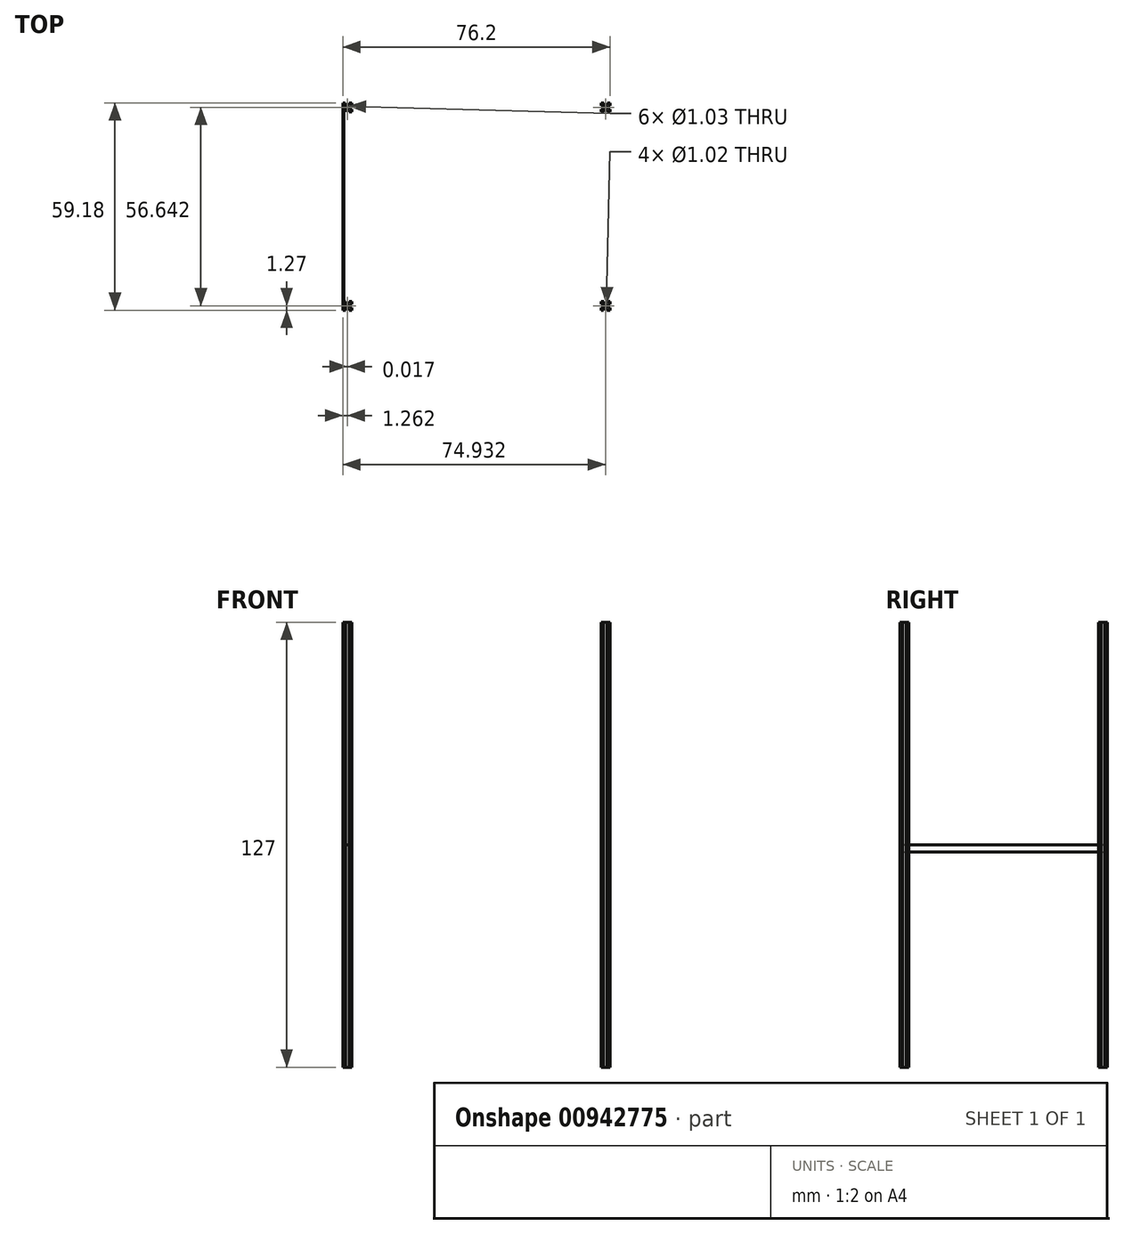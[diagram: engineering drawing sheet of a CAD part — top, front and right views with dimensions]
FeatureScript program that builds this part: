
annotation { "Feature Type Name" : "Feature", "Feature Type Description" : "" }
export const myFeature = defineFeature(function(context is Context, id is Id, definition is map)
    precondition{}
    {
        {
            var Q0;
            Q0=qCreatedBy(makeId("Top.planeOp"),FACE);
            var sketch = newSketch(context, id + "F0", { "sketchPlane" : qUnion([Q0])});
            skLineSegment(sketch, "E0.bottom", {"start": v(0, 0) * mm, "end": v(76.2, 0) * mm});
            skLineSegment(sketch, "E0.top", {"start": v(0, 59.18) * mm, "end": v(76.2, 59.18) * mm});
            skLineSegment(sketch, "E0.left", {"start": v(0, 0) * mm, "end": v(0, 59.18) * mm});
            skLineSegment(sketch, "E0.right", {"start": v(76.2, 0) * mm, "end": v(76.2, 59.18) * mm});
            skLineSegment(sketch, "E1.bottom", {"start": v(0, 59.18) * mm, "end": v(2.54, 59.18) * mm});
            skLineSegment(sketch, "E1.top", {"start": v(0, 56.64) * mm, "end": v(2.54, 56.64) * mm});
            skLineSegment(sketch, "E1.left", {"start": v(0, 59.18) * mm, "end": v(0, 56.64) * mm});
            skLineSegment(sketch, "E1.right", {"start": v(2.54, 59.18) * mm, "end": v(2.54, 56.64) * mm});
            skLineSegment(sketch, "E2.bottom", {"start": v(76.2, 59.18) * mm, "end": v(73.66, 59.18) * mm});
            skLineSegment(sketch, "E2.top", {"start": v(76.2, 56.64) * mm, "end": v(73.66, 56.64) * mm});
            skLineSegment(sketch, "E2.left", {"start": v(76.2, 59.18) * mm, "end": v(76.2, 56.64) * mm});
            skLineSegment(sketch, "E2.right", {"start": v(73.66, 59.18) * mm, "end": v(73.66, 56.64) * mm});
            skLineSegment(sketch, "E3.bottom", {"start": v(0, 0) * mm, "end": v(2.54, 0) * mm});
            skLineSegment(sketch, "E3.top", {"start": v(0, 2.54) * mm, "end": v(2.54, 2.54) * mm});
            skLineSegment(sketch, "E3.left", {"start": v(0, 0) * mm, "end": v(0, 2.54) * mm});
            skLineSegment(sketch, "E3.right", {"start": v(2.54, 0) * mm, "end": v(2.54, 2.54) * mm});
            skLineSegment(sketch, "E4.bottom", {"start": v(76.2, 0) * mm, "end": v(73.66, 0) * mm});
            skLineSegment(sketch, "E4.top", {"start": v(76.2, 2.54) * mm, "end": v(73.66, 2.54) * mm});
            skLineSegment(sketch, "E4.left", {"start": v(76.2, 0) * mm, "end": v(76.2, 2.54) * mm});
            skLineSegment(sketch, "E4.right", {"start": v(73.66, 0) * mm, "end": v(73.66, 2.54) * mm});
            skLineSegment(sketch, "E5", {"start": v(0, 57.91) * mm, "end": v(1.26, 57.91) * mm});
            skCircle(sketch, "E6", {"center": v(1.26, 57.91) * mm, "radius": 0.52 * mm});
            skLineSegment(sketch, "E7.bottom", {"start": v(0.74, 59.18) * mm, "end": v(1.79, 59.18) * mm});
            skLineSegment(sketch, "E7.top", {"start": v(0.74, 58.68) * mm, "end": v(1.79, 58.68) * mm});
            skLineSegment(sketch, "E7.left", {"start": v(0.74, 59.18) * mm, "end": v(0.74, 58.68) * mm});
            skLineSegment(sketch, "E7.right", {"start": v(1.79, 59.18) * mm, "end": v(1.79, 58.68) * mm});
            skLineSegment(sketch, "E8.bottom", {"start": v(2.54, 58.42) * mm, "end": v(2.04, 58.42) * mm});
            skLineSegment(sketch, "E8.top", {"start": v(2.54, 57.37) * mm, "end": v(2.04, 57.37) * mm});
            skLineSegment(sketch, "E8.left", {"start": v(2.54, 58.42) * mm, "end": v(2.54, 57.37) * mm});
            skLineSegment(sketch, "E8.right", {"start": v(2.04, 58.42) * mm, "end": v(2.04, 57.37) * mm});
            skLineSegment(sketch, "E9.bottom", {"start": v(0.74, 56.64) * mm, "end": v(1.79, 56.64) * mm});
            skLineSegment(sketch, "E9.top", {"start": v(0.74, 57.14) * mm, "end": v(1.79, 57.14) * mm});
            skLineSegment(sketch, "E9.left", {"start": v(0.74, 56.64) * mm, "end": v(0.74, 57.14) * mm});
            skLineSegment(sketch, "E9.right", {"start": v(1.79, 56.64) * mm, "end": v(1.79, 57.14) * mm});
            skLineSegment(sketch, "E10.bottom", {"start": v(0, 57.37) * mm, "end": v(0.5, 57.37) * mm});
            skLineSegment(sketch, "E10.top", {"start": v(0, 58.4) * mm, "end": v(0.5, 58.4) * mm});
            skLineSegment(sketch, "E10.left", {"start": v(0, 57.37) * mm, "end": v(0, 58.4) * mm});
            skLineSegment(sketch, "E10.right", {"start": v(0.5, 57.37) * mm, "end": v(0.5, 58.4) * mm});
            skLineSegment(sketch, "E11", {"start": v(73.66, 57.91) * mm, "end": v(74.93, 57.91) * mm});
            skCircle(sketch, "E12", {"center": v(74.93, 57.91) * mm, "radius": 0.5 * mm});
            skLineSegment(sketch, "E13.bottom", {"start": v(76.2, 58.39) * mm, "end": v(75.7, 58.39) * mm});
            skLineSegment(sketch, "E13.top", {"start": v(76.2, 57.38) * mm, "end": v(75.7, 57.38) * mm});
            skLineSegment(sketch, "E13.left", {"start": v(76.2, 58.39) * mm, "end": v(76.2, 57.38) * mm});
            skLineSegment(sketch, "E13.right", {"start": v(75.7, 58.39) * mm, "end": v(75.7, 57.38) * mm});
            skLineSegment(sketch, "E14.bottom", {"start": v(73.66, 57.38) * mm, "end": v(74.16, 57.38) * mm});
            skLineSegment(sketch, "E14.top", {"start": v(73.66, 58.4) * mm, "end": v(74.16, 58.4) * mm});
            skLineSegment(sketch, "E14.left", {"start": v(73.66, 57.38) * mm, "end": v(73.66, 58.4) * mm});
            skLineSegment(sketch, "E14.right", {"start": v(74.16, 57.38) * mm, "end": v(74.16, 58.4) * mm});
            skLineSegment(sketch, "E15", {"start": v(73.66, 1.27) * mm, "end": v(74.93, 1.27) * mm});
            skCircle(sketch, "E16", {"center": v(74.93, 1.27) * mm, "radius": 0.51 * mm});
            skLineSegment(sketch, "E17.bottom", {"start": v(76.2, 1.75) * mm, "end": v(75.7, 1.75) * mm});
            skLineSegment(sketch, "E17.top", {"start": v(76.2, 0.73) * mm, "end": v(75.7, 0.73) * mm});
            skLineSegment(sketch, "E17.left", {"start": v(76.2, 1.75) * mm, "end": v(76.2, 0.73) * mm});
            skLineSegment(sketch, "E17.right", {"start": v(75.7, 1.75) * mm, "end": v(75.7, 0.73) * mm});
            skLineSegment(sketch, "E18.bottom", {"start": v(73.66, 1.75) * mm, "end": v(74.16, 1.75) * mm});
            skLineSegment(sketch, "E18.top", {"start": v(73.66, 0.73) * mm, "end": v(74.16, 0.73) * mm});
            skLineSegment(sketch, "E18.left", {"start": v(73.66, 1.75) * mm, "end": v(73.66, 0.73) * mm});
            skLineSegment(sketch, "E18.right", {"start": v(74.16, 1.75) * mm, "end": v(74.16, 0.73) * mm});
            skLineSegment(sketch, "E19", {"start": v(0, 1.27) * mm, "end": v(1.28, 1.27) * mm});
            skCircle(sketch, "E20", {"center": v(1.28, 1.27) * mm, "radius": 0.51 * mm});
            skLineSegment(sketch, "E21.bottom", {"start": v(0.77, 2.54) * mm, "end": v(1.79, 2.54) * mm});
            skLineSegment(sketch, "E21.top", {"start": v(0.77, 2.04) * mm, "end": v(1.79, 2.04) * mm});
            skLineSegment(sketch, "E21.left", {"start": v(0.77, 2.54) * mm, "end": v(0.77, 2.04) * mm});
            skLineSegment(sketch, "E21.right", {"start": v(1.79, 2.54) * mm, "end": v(1.79, 2.04) * mm});
            skLineSegment(sketch, "E22.bottom", {"start": v(1.79, 0) * mm, "end": v(0.78, 0) * mm});
            skLineSegment(sketch, "E22.top", {"start": v(1.79, 0.5) * mm, "end": v(0.78, 0.5) * mm});
            skLineSegment(sketch, "E22.left", {"start": v(1.79, 0) * mm, "end": v(1.79, 0.5) * mm});
            skLineSegment(sketch, "E22.right", {"start": v(0.78, 0) * mm, "end": v(0.78, 0.5) * mm});
            skLineSegment(sketch, "E23.bottom", {"start": v(2.54, 1.75) * mm, "end": v(2.03, 1.75) * mm});
            skLineSegment(sketch, "E23.top", {"start": v(2.54, 0.74) * mm, "end": v(2.03, 0.74) * mm});
            skLineSegment(sketch, "E23.left", {"start": v(2.54, 1.75) * mm, "end": v(2.54, 0.74) * mm});
            skLineSegment(sketch, "E23.right", {"start": v(2.03, 1.75) * mm, "end": v(2.03, 0.74) * mm});
            skLineSegment(sketch, "E24.bottom", {"start": v(0, 0.74) * mm, "end": v(0.52, 0.74) * mm});
            skLineSegment(sketch, "E24.top", {"start": v(0, 1.75) * mm, "end": v(0.52, 1.75) * mm});
            skLineSegment(sketch, "E24.left", {"start": v(0, 0.74) * mm, "end": v(0, 1.75) * mm});
            skLineSegment(sketch, "E24.right", {"start": v(0.52, 0.74) * mm, "end": v(0.52, 1.75) * mm});
            skLineSegment(sketch, "E25", {"start": v(61.7, 59.18) * mm, "end": v(73.66, 59.18) * mm});
            skLineSegment(sketch, "E26", {"start": v(73.66, 58.4) * mm, "end": v(73.66, 59.18) * mm});
            skLineSegment(sketch, "E27", {"start": v(76.2, 57.38) * mm, "end": v(76.2, 56.64) * mm});
            skLineSegment(sketch, "E28", {"start": v(73.66, 59.18) * mm, "end": v(76.2, 59.18) * mm});
            skLineSegment(sketch, "E29.bottom", {"start": v(74.44, 59.18) * mm, "end": v(75.44, 59.18) * mm});
            skLineSegment(sketch, "E29.top", {"start": v(74.44, 58.67) * mm, "end": v(75.44, 58.67) * mm});
            skLineSegment(sketch, "E29.left", {"start": v(74.44, 59.18) * mm, "end": v(74.44, 58.67) * mm});
            skLineSegment(sketch, "E29.right", {"start": v(75.44, 59.18) * mm, "end": v(75.44, 58.67) * mm});
            skLineSegment(sketch, "E30.bottom", {"start": v(75.44, 56.64) * mm, "end": v(74.44, 56.64) * mm});
            skLineSegment(sketch, "E30.top", {"start": v(75.44, 57.16) * mm, "end": v(74.44, 57.16) * mm});
            skLineSegment(sketch, "E30.left", {"start": v(75.44, 56.64) * mm, "end": v(75.44, 57.16) * mm});
            skLineSegment(sketch, "E30.right", {"start": v(74.44, 56.64) * mm, "end": v(74.44, 57.16) * mm});
            skPoint(sketch, "E31.right.end.orphan", {"position": v(62.7, 58.68) * mm});
            skPoint(sketch, "E32.left.start.orphan", {"position": v(62.7, 56.64) * mm});
            skLineSegment(sketch, "E33.bottom", {"start": v(74.46, 2.54) * mm, "end": v(75.45, 2.54) * mm});
            skLineSegment(sketch, "E33.top", {"start": v(74.46, 2.04) * mm, "end": v(75.45, 2.04) * mm});
            skLineSegment(sketch, "E33.left", {"start": v(74.46, 2.54) * mm, "end": v(74.46, 2.04) * mm});
            skLineSegment(sketch, "E33.right", {"start": v(75.45, 2.54) * mm, "end": v(75.45, 2.04) * mm});
            skLineSegment(sketch, "E34.bottom", {"start": v(75.4, 0) * mm, "end": v(74.38, 0) * mm});
            skLineSegment(sketch, "E34.top", {"start": v(75.4, 0.52) * mm, "end": v(74.38, 0.52) * mm});
            skLineSegment(sketch, "E34.left", {"start": v(75.4, 0) * mm, "end": v(75.4, 0.52) * mm});
            skLineSegment(sketch, "E34.right", {"start": v(74.38, 0) * mm, "end": v(74.38, 0.52) * mm});
            skPoint(sketch, "E35.right.end.orphan", {"position": v(62.72, 2.04) * mm});
            skPoint(sketch, "E36.left.start.orphan", {"position": v(62.72, 0) * mm});
            skSolve(sketch);
        }
        {
            var Q0;
            Q0=makeQuery(id+"F0.imprint","IMPRINT",FACE,{"disambiguationData":[TD([[makeQuery(id+"F0.imprint","IMPRINT",EDGE,{"derivedFrom":sQuery(id+"F0.wireOp",EDGE,"E12")}),-1.0]])]});
            var Q1;
            Q1=makeQuery(id+"F0.imprint","IMPRINT",FACE,{"disambiguationData":[TD([[makeQuery(id+"F0.imprint","IMPRINT",EDGE,{"derivedFrom":sQuery(id+"F0.wireOp",EDGE,"E16")}),-1.0]])]});
            var Q2;
            Q2=makeQuery(id+"F0.imprint","IMPRINT",FACE,{"disambiguationData":[TD([[makeQuery(id+"F0.imprint","IMPRINT",EDGE,{"derivedFrom":sQuery(id+"F0.wireOp",EDGE,"E20")}),-1.0]])]});
            extrude(context, id + "F1", {"entities" : qUnion([Q0, Q1, Q2]), "depth" : 127 * mm, "offsetDistance" : 25.4 * mm});
        }
        {
            var Q0;
            Q0=qCreatedBy(makeId("Right.planeOp"),FACE);
            var sketch = newSketch(context, id + "F2", { "sketchPlane" : qUnion([Q0])});
            skLineSegment(sketch, "E37", {"start": v(0, 0) * mm, "end": v(0, 127) * mm});
            skLineSegment(sketch, "E38", {"start": v(0, 127) * mm, "end": v(0, 63.5) * mm});
            skLineSegment(sketch, "E39.bottom", {"start": v(0, 63.5) * mm, "end": v(59.18, 63.5) * mm});
            skLineSegment(sketch, "E39.top", {"start": v(0, 61.44) * mm, "end": v(59.18, 61.44) * mm});
            skLineSegment(sketch, "E39.left", {"start": v(0, 63.5) * mm, "end": v(0, 61.44) * mm});
            skLineSegment(sketch, "E39.right", {"start": v(59.18, 63.5) * mm, "end": v(59.18, 61.44) * mm});
            skLineSegment(sketch, "E40", {"start": v(0, 0) * mm, "end": v(0, 32.08) * mm});
            skLineSegment(sketch, "E41.bottom", {"start": v(0, 32.08) * mm, "end": v(76.4, 32.08) * mm});
            skLineSegment(sketch, "E41.top", {"start": v(0, 28.66) * mm, "end": v(76.4, 28.66) * mm});
            skLineSegment(sketch, "E41.left", {"start": v(0, 32.08) * mm, "end": v(0, 28.66) * mm});
            skLineSegment(sketch, "E41.right", {"start": v(76.4, 32.08) * mm, "end": v(76.4, 28.66) * mm});
            skSolve(sketch);
        }
        {
            var Q0;
            {var subQ0=sQuery(id+"F2.wireOp",EDGE,"E39.bottom");Q0=makeQuery(id+"F2.imprint","IMPRINT",FACE,{"disambiguationData":[TD([[makeQuery(id+"F2.imprint","IMPRINT",EDGE,{"derivedFrom":subQ0}),-1.0]])]});}
            extrude(context, id + "F3", {"entities" : qUnion([Q0]), "depth" : 0.25 * mm, "offsetDistance" : 25.4 * mm});
        }
        {
            var Q0;
            Q0=makeQuery(id+"F0.imprint","IMPRINT",FACE,{"disambiguationData":[TD([[makeQuery(id+"F0.imprint","IMPRINT",EDGE,{"derivedFrom":sQuery(id+"F0.wireOp",EDGE,"E20")}),-1.0]])]});
            var Q1;
            Q1=makeQuery(id+"F0.imprint","IMPRINT",FACE,{"disambiguationData":[TD([[makeQuery(id+"F0.imprint","IMPRINT",EDGE,{"derivedFrom":sQuery(id+"F0.wireOp",EDGE,"E6")}),-1.0]])]});
            extrude(context, id + "F4", {"entities" : qUnion([Q0, Q1]), "depth" : 63.5 * mm, "offsetDistance" : 25.4 * mm});
        }
    });
